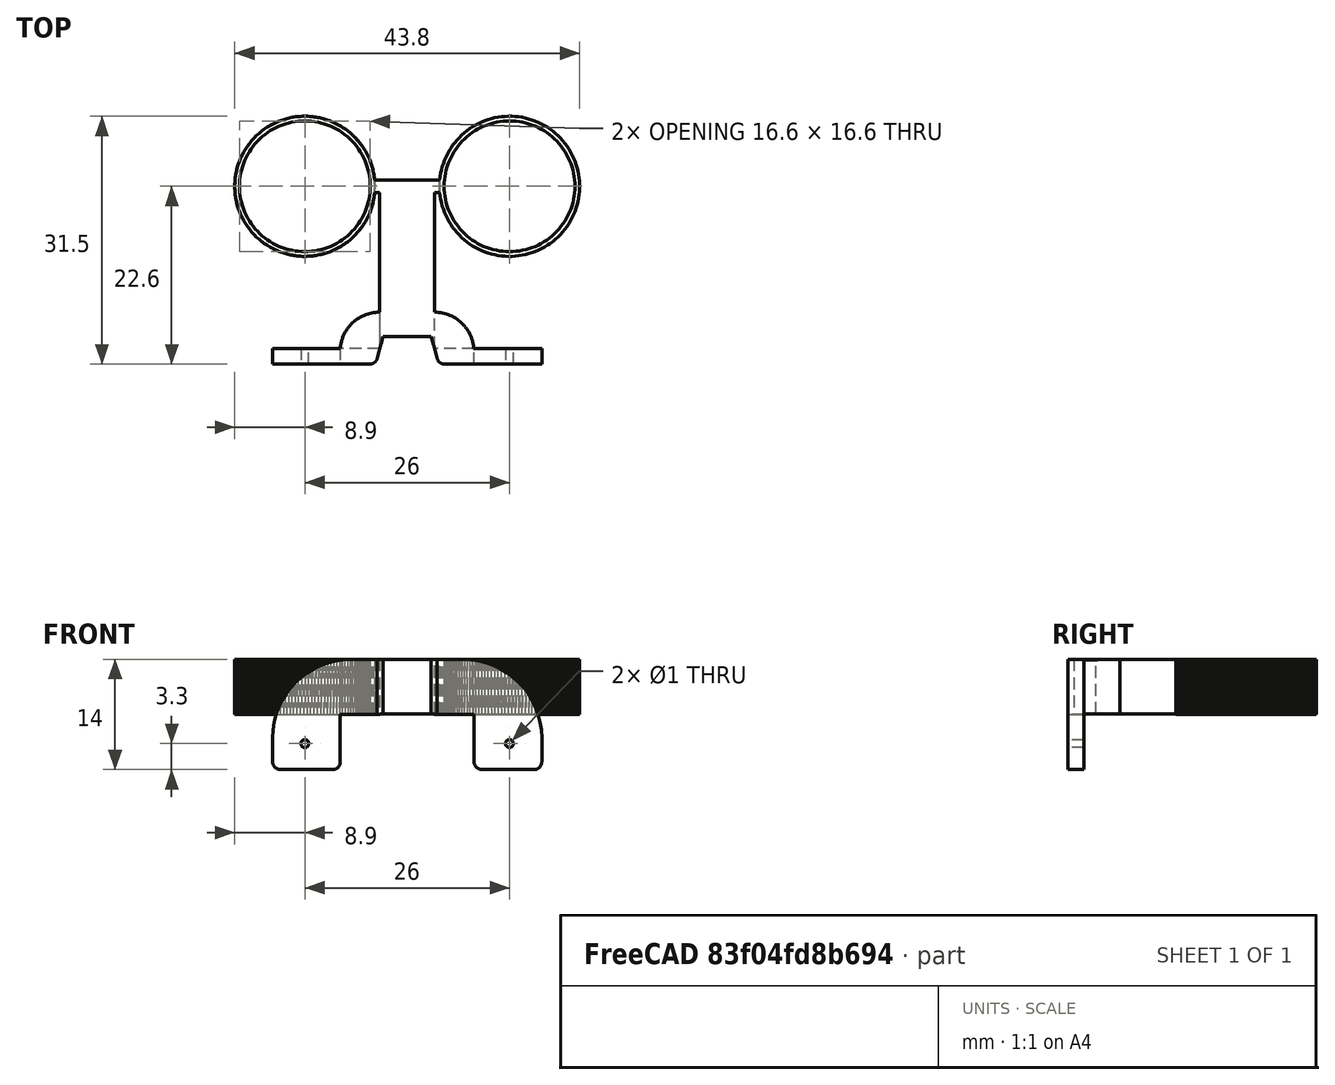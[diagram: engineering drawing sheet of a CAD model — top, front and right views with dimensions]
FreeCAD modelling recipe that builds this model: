
FCSTD DOCUMENT  (FreeCAD 1.0R39109 (Git))
Label: hc-sr04 mount
License: All rights reserved
LicenseURL: https://en.wikipedia.org/wiki/All_rights_reserved
objects: Sketcher::SketchObject×8, PartDesign::Fillet×5, PartDesign::Pad×3, PartDesign::Pocket×3, Part::Feature×2, PartDesign::Revolution×2, Mesh::Feature×1, Part::Refine×1, PartDesign::FeatureBase×1, PartDesign::Body×1
note: 61 computed .brp shape members not serialized (recipe doc carries the construction recipe); baked Part::Feature solids carry a one-line shape summary decoded from their .brp

FEATURE [Mesh::Feature] mount
FEATURE [Part::Feature] mount001
  shape: bbox 43.8 x 29.69 x 7 mm, 2726 faces, 0 solids (baked)
FEATURE [Part::Refine] mount002
  Source = -> mount001
FEATURE [Part::Feature] mount002_solid  label="mount002 (Solid)"
  shape: bbox 43.8 x 29.69 x 7 mm, 1196 faces (baked)
FEATURE [PartDesign::FeatureBase] BaseFeature
  BaseFeature = -> mount002_solid
  Suppressed = false
FEATURE [Sketcher::SketchObject] Sketch
  ArcFitTolerance = 1e-06
  AttachmentSupport = -> [BaseFeature]
  FullyConstrained = true
  MakeInternals = false
  MapMode = 5
  Placement = pos=(0,0,12) rot=(0,0,1;0rad)
  sketch-geometry (9):
    g0: LineSegment StartX=0 StartY=-20.6 StartZ=0 EndX=0 EndY=-22.6 EndZ=0
    g1: LineSegment StartX=0 StartY=-22.6 StartZ=0 EndX=17.1 EndY=-22.6 EndZ=0
    g2: LineSegment StartX=17.1 StartY=-22.6 StartZ=0 EndX=17.1 EndY=-20.6 EndZ=0
    g3: LineSegment StartX=17.1 StartY=-20.6 StartZ=0 EndX=0 EndY=-20.6 EndZ=0
    g4: LineSegment [constr] StartX=0 StartY=0 StartZ=0 EndX=0 EndY=-20.6 EndZ=0
    g5: LineSegment StartX=0 StartY=-20.6 StartZ=0 EndX=-17.1 EndY=-20.6 EndZ=0
    g6: LineSegment StartX=-17.1 StartY=-20.6 StartZ=0 EndX=-17.1 EndY=-22.6 EndZ=0
    g7: LineSegment StartX=-17.1 StartY=-22.6 StartZ=0 EndX=0 EndY=-22.6 EndZ=0
    g8: LineSegment StartX=0 StartY=-22.6 StartZ=0 EndX=0 EndY=-20.6 EndZ=0
  constraints (25):
    c: Coincident(g0,g1)
    c: Coincident(g1,g2)
    c: Coincident(g2,g3)
    c: Coincident(g3,g0)
    c: Vertical(g0)
    c: Vertical(g2)
    c: Horizontal(g1)
    c: Horizontal(g3)
    c: Distance(g0,g2) = 17.1
    c: Distance(g1,g3) = 2
    c: PointOnObject(g0,g-2)
    c: Distance(g4) = 20.6
    c: Coincident(g4,g-1)
    c: Coincident(g0,g4)
    c: Coincident(g5,g6)
    c: Coincident(g6,g7)
    c: Coincident(g7,g8)
    c: Coincident(g8,g5)
    c: Horizontal(g5)
    c: Horizontal(g7)
    c: Vertical(g6)
    c: Vertical(g8)
    c: Distance(g6,g8) = 17.1
    c: Distance(g5,g7) = 2
    c: Coincident(g5,g0)
FEATURE [PartDesign::Pad] Pad  label="Base"
  BaseFeature = -> BaseFeature
  Direction = (0,0,1)
  Length = 7
  Length2 = 10
  Profile = -> Sketch [Edge5,Edge6,Edge7,Edge2,Edge3,Edge4]
  ReferenceAxis = -> Sketch [N_Axis]
  Refine = true
  Reversed = true
  Suppressed = false
  Type = 0
FEATURE [Sketcher::SketchObject] Sketch001
  ArcFitTolerance = 1e-06
  AttachmentSupport = -> [Pad]
  FullyConstrained = true
  MakeInternals = false
  MapMode = 5
  Placement = pos=(-3.51934,0,0) rot=(0.57735,-0.57735,-0.57735;2.0944rad)
  sketch-geometry (6):
    g0: LineSegment [constr] StartX=0 StartY=0 StartZ=0 EndX=21 EndY=0 EndZ=0
    g1: LineSegment [constr] StartX=21 StartY=0 StartZ=0 EndX=21 EndY=5.1 EndZ=0
    g2: LineSegment StartX=21 StartY=5.1 StartZ=0 EndX=21 EndY=12 EndZ=0
    g3: LineSegment StartX=21 StartY=12 StartZ=0 EndX=16 EndY=12 EndZ=0
    g4: LineSegment StartX=16 StartY=12 StartZ=0 EndX=16 EndY=5.1 EndZ=0
    g5: LineSegment StartX=16 StartY=5.1 StartZ=0 EndX=21 EndY=5.1 EndZ=0
  constraints (17):
    c: Distance(g0) = 21
    c: Coincident(g0,g-1)
    c: PointOnObject(g0,g-1)
    c: Distance(g1) = 5.1
    c: Coincident(g1,g0)
    c: Vertical(g1)
    c: Coincident(g2,g3)
    c: Coincident(g3,g4)
    c: Coincident(g4,g5)
    c: Coincident(g5,g2)
    c: Vertical(g2)
    c: Vertical(g4)
    c: Horizontal(g3)
    c: Horizontal(g5)
    c: Distance(g2,g4) = 5
    c: Distance(g3,g5) = 6.9
    c: Coincident(g2,g1)
FEATURE [PartDesign::Revolution] Revolution
  Angle = 90
  Angle2 = 60
  Axis = (0,0,5.1)
  Base = (-3.51934,-21,0)
  BaseFeature = -> Pad
  Profile = -> Sketch001
  ReferenceAxis = -> Sketch001 [Axis1]
  Refine = true
  Suppressed = false
  Type = 0
FEATURE [Sketcher::SketchObject] Sketch002
  ArcFitTolerance = 1e-06
  AttachmentSupport = -> [Revolution]
  FullyConstrained = true
  MakeInternals = false
  MapMode = 5
  Placement = pos=(3.48066,0,0) rot=(0.57735,0.57735,0.57735;2.0944rad)
  sketch-geometry (6):
    g0: LineSegment [constr] StartX=0 StartY=0 StartZ=0 EndX=-21 EndY=0 EndZ=0
    g1: LineSegment [constr] StartX=-21 StartY=0 StartZ=0 EndX=-21 EndY=5.1 EndZ=0
    g2: LineSegment StartX=-21 StartY=5.1 StartZ=0 EndX=-16 EndY=5.1 EndZ=0
    g3: LineSegment StartX=-16 StartY=5.1 StartZ=0 EndX=-16 EndY=12 EndZ=0
    g4: LineSegment StartX=-16 StartY=12 StartZ=0 EndX=-21 EndY=12 EndZ=0
    g5: LineSegment StartX=-21 StartY=12 StartZ=0 EndX=-21 EndY=5.1 EndZ=0
  constraints (17):
    c: Distance(g0) = 21
    c: Coincident(g0,g-1)
    c: PointOnObject(g0,g-1)
    c: Distance(g1) = 5.1
    c: Coincident(g1,g0)
    c: Vertical(g1)
    c: Coincident(g2,g3)
    c: Coincident(g3,g4)
    c: Coincident(g4,g5)
    c: Coincident(g5,g2)
    c: Horizontal(g2)
    c: Horizontal(g4)
    c: Vertical(g3)
    c: Vertical(g5)
    c: Distance(g3,g5) = 5
    c: Distance(g2,g4) = 6.9
    c: Coincident(g2,g1)
FEATURE [PartDesign::Revolution] Revolution001
  Angle = 90
  Angle2 = 60
  Axis = (0,0,5.1)
  Base = (3.48066,-21,0)
  BaseFeature = -> Revolution
  Profile = -> Sketch002
  ReferenceAxis = -> Sketch002 [Axis1]
  Refine = true
  Reversed = true
  Suppressed = false
  Type = 0
FEATURE [Sketcher::SketchObject] Sketch003
  ArcFitTolerance = 1e-06
  AttachmentSupport = -> [Revolution001]
  FullyConstrained = true
  MakeInternals = false
  MapMode = 5
  Placement = pos=(0,-22.6,0) rot=(1,0,0;1.5708rad)
  sketch-geometry (6):
    g0: LineSegment [constr] StartX=0 StartY=0 StartZ=0 EndX=0 EndY=3 EndZ=0
    g1: LineSegment [constr] StartX=0 StartY=3 StartZ=0 EndX=4 EndY=3 EndZ=0
    g2: LineSegment StartX=4 StartY=3 StartZ=0 EndX=4 EndY=14 EndZ=0
    g3: LineSegment StartX=4 StartY=14 StartZ=0 EndX=-4 EndY=14 EndZ=0
    g4: LineSegment StartX=-4 StartY=14 StartZ=0 EndX=-4 EndY=3 EndZ=0
    g5: LineSegment StartX=-4 StartY=3 StartZ=0 EndX=4 EndY=3 EndZ=0
  constraints (17):
    c: Distance(g0) = 3
    c: Coincident(g0,g-1)
    c: PointOnObject(g0,g-2)
    c: Distance(g1) = 4
    c: Coincident(g1,g0)
    c: Horizontal(g1)
    c: Coincident(g2,g3)
    c: Coincident(g3,g4)
    c: Coincident(g4,g5)
    c: Coincident(g5,g2)
    c: Vertical(g2)
    c: Vertical(g4)
    c: Horizontal(g3)
    c: Horizontal(g5)
    c: Distance(g2,g4) = 8
    c: Distance(g3,g5) = 11
    c: Coincident(g2,g1)
FEATURE [PartDesign::Pocket] Pocket
  BaseFeature = -> Revolution001
  Direction = (0,1,-2e-16)
  Length = 3.5
  Length2 = 5
  Profile = -> Sketch003
  ReferenceAxis = -> Sketch003 [N_Axis]
  Refine = true
  Suppressed = false
  TaperAngle = -15
  Type = 0
FEATURE [Sketcher::SketchObject] Sketch004
  ArcFitTolerance = 1e-06
  AttachmentSupport = -> [Pocket]
  FullyConstrained = true
  MakeInternals = false
  MapMode = 5
  Placement = pos=(0,-19.1,7.4e-15) rot=(1,0,0;1.5708rad)
  sketch-geometry (2):
    g0: LineSegment [constr] StartX=0 StartY=0 StartZ=0 EndX=0 EndY=8.5 EndZ=0
    g1: Circle CenterX=0 CenterY=8.5 CenterZ=0 NormalX=0 NormalY=0 NormalZ=1 AngleXU=0 Radius=3.1
  constraints (5):
    c: Distance(g0) = 8.5
    c: Coincident(g0,g-1)
    c: PointOnObject(g0,g-2)
    c: Diameter(g1) = 6.2
    c: Coincident(g1,g0)
FEATURE [PartDesign::Pad] Pad001
  BaseFeature = -> Pocket
  Direction = (0,-1,2e-16)
  Length = 10
  Length2 = 10
  Profile = -> Sketch004
  ReferenceAxis = -> Sketch004 [N_Axis]
  Refine = true
  Reversed = true
  Suppressed = false
  Type = 0
FEATURE [Sketcher::SketchObject] Sketch005
  ArcFitTolerance = 1e-06
  AttachmentSupport = -> [Pad001]
  FullyConstrained = true
  MakeInternals = false
  MapMode = 5
  Placement = pos=(0,-22.6,0) rot=(1,0,0;1.5708rad)
  sketch-geometry (5):
    g0: LineSegment [constr] StartX=0 StartY=0 StartZ=0 EndX=13 EndY=0 EndZ=0
    g1: LineSegment [constr] StartX=13 StartY=0 StartZ=0 EndX=13 EndY=1.3 EndZ=0
    g2: Circle CenterX=13 CenterY=1.3 CenterZ=0 NormalX=0 NormalY=0 NormalZ=1 AngleXU=0 Radius=0.5
    g3: LineSegment [constr] StartX=13 StartY=1.3 StartZ=0 EndX=-13 EndY=1.3 EndZ=0
    g4: Circle CenterX=-13 CenterY=1.3 CenterZ=0 NormalX=0 NormalY=0 NormalZ=1 AngleXU=0 Radius=0.5
  constraints (13):
    c: Distance(g0) = 13
    c: Coincident(g0,g-1)
    c: PointOnObject(g0,g-1)
    c: Distance(g1) = 1.3
    c: Coincident(g1,g0)
    c: Vertical(g1)
    c: Diameter(g2) = 1
    c: Coincident(g2,g1)
    c: Distance(g3) = 26
    c: Coincident(g3,g1)
    c: Horizontal(g3)
    c: Diameter(g4) = 1
    c: Coincident(g4,g3)
FEATURE [PartDesign::Pocket] Pocket001
  BaseFeature = -> Pad001
  Direction = (0,1,-2e-16)
  Length = 3
  Length2 = 5
  Profile = -> Sketch005
  ReferenceAxis = -> Sketch005 [N_Axis]
  Refine = true
  Suppressed = false
  Type = 0
FEATURE [Sketcher::SketchObject] Sketch006
  ArcFitTolerance = 1e-06
  AttachmentSupport = -> [Pocket001]
  ExternalGeometry = -> [Pocket001]
  FullyConstrained = true
  MakeInternals = false
  MapMode = 5
  Placement = pos=(0,0,5) rot=(1,0,0;3.14159rad)
  sketch-geometry (8):
    g0: LineSegment StartX=17.1 StartY=20.6 StartZ=0 EndX=17.1 EndY=22.6 EndZ=0
    g1: LineSegment StartX=17.1 StartY=22.6 StartZ=0 EndX=8.5 EndY=22.6 EndZ=0
    g2: LineSegment StartX=8.5 StartY=22.6 StartZ=0 EndX=8.5 EndY=20.6 EndZ=0
    g3: LineSegment StartX=8.5 StartY=20.6 StartZ=0 EndX=17.1 EndY=20.6 EndZ=0
    g4: LineSegment StartX=-17.1 StartY=20.6 StartZ=0 EndX=-8.5 EndY=20.6 EndZ=0
    g5: LineSegment StartX=-8.5 StartY=20.6 StartZ=0 EndX=-8.5 EndY=22.6 EndZ=0
    g6: LineSegment StartX=-8.5 StartY=22.6 StartZ=0 EndX=-17.1 EndY=22.6 EndZ=0
    g7: LineSegment StartX=-17.1 StartY=22.6 StartZ=0 EndX=-17.1 EndY=20.6 EndZ=0
  constraints (22):
    c: Coincident(g0,g1)
    c: Coincident(g1,g2)
    c: Coincident(g2,g3)
    c: Coincident(g3,g0)
    c: Vertical(g0)
    c: Vertical(g2)
    c: Horizontal(g1)
    c: Horizontal(g3)
    c: Distance(g0,g2) = 8.6
    c: Distance(g1,g3) = 2
    c: Coincident(g0,g-6)
    c: Coincident(g4,g5)
    c: Coincident(g5,g6)
    c: Coincident(g6,g7)
    c: Coincident(g7,g4)
    c: Horizontal(g4)
    c: Horizontal(g6)
    c: Vertical(g5)
    c: Vertical(g7)
    c: Distance(g5,g7) = 8.6
    c: Distance(g4,g6) = 2
    c: Coincident(g4,g-4)
FEATURE [PartDesign::Pad] Pad002
  BaseFeature = -> Pocket001
  Direction = (0,0,-1)
  Length = 7
  Length2 = 10
  Profile = -> Sketch006
  ReferenceAxis = -> Sketch006 [N_Axis]
  Refine = true
  Suppressed = false
  Type = 0
FEATURE [PartDesign::Pocket] Pocket002
  BaseFeature = -> Pad002
  Direction = (0,1,-2e-16)
  Length = 5
  Length2 = 5
  Profile = -> Sketch005
  ReferenceAxis = -> Sketch005 [N_Axis]
  Refine = true
  Suppressed = false
  Type = 0
FEATURE [Sketcher::SketchObject] Sketch007
  ArcFitTolerance = 1e-06
  AttachmentSupport = -> [Pocket002]
  ExternalGeometry = -> [Pocket002]
  FullyConstrained = true
  MakeInternals = false
  MapMode = 5
  Placement = pos=(-5.7e-15,-20.6,0) rot=(0,0.707107,0.707107;3.14159rad)
FEATURE [PartDesign::Fillet] Fillet
  Base = -> Pocket002 [Edge24]
  BaseFeature = -> Pocket002
  Radius = 1
  Refine = true
  SupportTransform = false
  Suppressed = false
  UseAllEdges = false
FEATURE [PartDesign::Fillet] Fillet001
  Base = -> Fillet [Edge1585]
  BaseFeature = -> Fillet
  Radius = 1
  Refine = true
  SupportTransform = false
  Suppressed = false
  UseAllEdges = false
FEATURE [PartDesign::Fillet] Fillet002
  Base = -> Fillet001 [Edge555,Edge11]
  BaseFeature = -> Fillet001
  Radius = 1
  Refine = true
  SupportTransform = false
  Suppressed = false
  UseAllEdges = false
FEATURE [PartDesign::Fillet] Fillet003
  Base = -> Fillet002 [Edge23,Edge18]
  BaseFeature = -> Fillet002
  Radius = 10
  Refine = true
  SupportTransform = false
  Suppressed = false
  UseAllEdges = false
FEATURE [PartDesign::Fillet] Fillet004
  Base = -> Fillet003 [Edge6,Edge562]
  BaseFeature = -> Fillet003
  Radius = 1
  Refine = true
  SupportTransform = false
  Suppressed = false
  UseAllEdges = false
FEATURE [PartDesign::Body] Body
  AllowCompound = false
  BaseFeature = -> mount002_solid
  Group = -> [BaseFeature,Sketch,Pad,Sketch001,Revolution,Sketch002,Revolution001,Sketch003,Pocket,Sketch004,Pad001,Sketch005,Pocket001,Sketch006,Pad002,Pocket002,Sketch007,Fillet,Fillet001,Fillet002,Fillet003,Fillet004]
  Origin = -> Origin
  Tip = -> Fillet004
